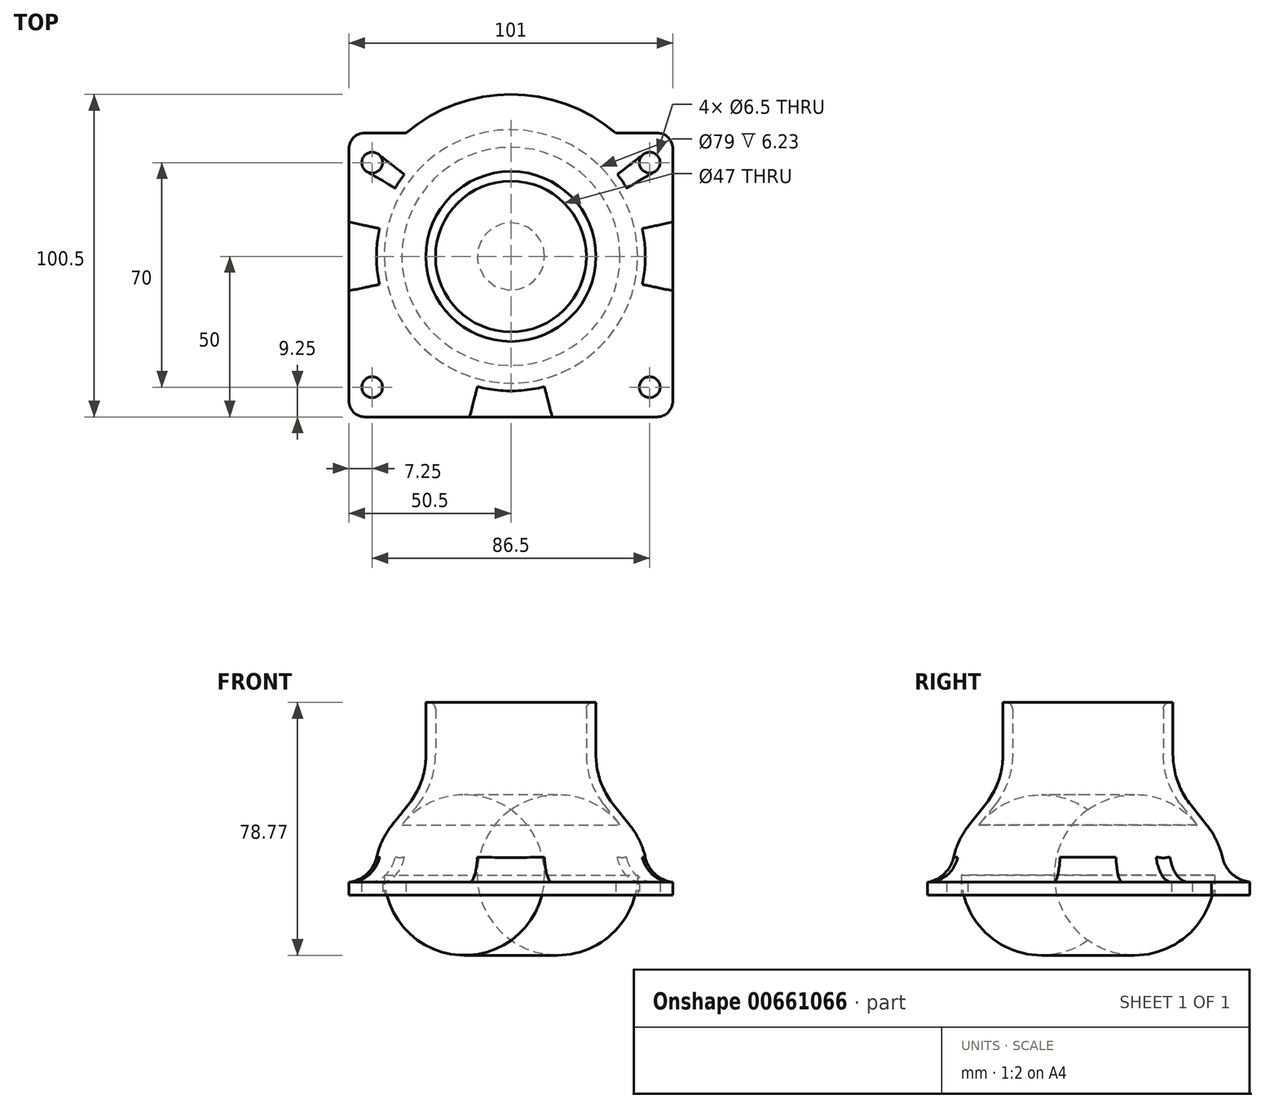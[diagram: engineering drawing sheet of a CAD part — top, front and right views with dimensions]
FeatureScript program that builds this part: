
annotation { "Feature Type Name" : "Feature", "Feature Type Description" : "" }
export const myFeature = defineFeature(function(context is Context, id is Id, definition is map)
    precondition{}
    {
        {
            assignVariable(context, id + "F0", {"name" : "baseTh", "anyValue" : 4});
        }
        {
            var Q0;
            Q0=qCreatedBy(makeId("Top.planeOp"),FACE);
            var sketch = newSketch(context, id + "F1", { "sketchPlane" : qUnion([Q0])});
            skLineSegment(sketch, "E0.bottom", {"start": v(45.5, -44.25) * mm, "end": v(-45.5, -44.25) * mm});
            skLineSegment(sketch, "E0.top", {"start": v(45.5, 44.25) * mm, "end": v(32.68, 44.25) * mm});
            skLineSegment(sketch, "E0.left", {"start": v(50.5, -39.25) * mm, "end": v(50.5, 39.25) * mm});
            skLineSegment(sketch, "E0.right", {"start": v(-50.5, -39.25) * mm, "end": v(-50.5, 39.25) * mm});
            skPoint(sketch, "E0.middle", {"position": v(0, 0) * mm});
            skLineSegment(sketch, "E1.bottom", {"start": v(43.25, -35) * mm, "end": v(-43.25, -35) * mm, "construction": true});
            skLineSegment(sketch, "E1.top", {"start": v(43.25, 35) * mm, "end": v(-43.25, 35) * mm, "construction": true});
            skLineSegment(sketch, "E1.left", {"start": v(43.25, -35) * mm, "end": v(43.25, 35) * mm, "construction": true});
            skLineSegment(sketch, "E1.right", {"start": v(-43.25, -35) * mm, "end": v(-43.25, 35) * mm, "construction": true});
            skCircle(sketch, "E2", {"center": v(-43.25, 35) * mm, "radius": 3.25 * mm});
            skCircle(sketch, "E3", {"center": v(-43.25, -35) * mm, "radius": 3.25 * mm});
            skCircle(sketch, "E4", {"center": v(43.25, -35) * mm, "radius": 3.25 * mm});
            skCircle(sketch, "E5", {"center": v(43.25, 35) * mm, "radius": 3.25 * mm});
            skLineSegment(sketch, "E6", {"start": v(0, -35) * mm, "end": v(0, 5.75) * mm, "construction": true});
            skCircle(sketch, "E7", {"center": v(0, 5.75) * mm, "radius": 39.5 * mm});
            skCircle(sketch, "E8", {"center": v(0, 5.75) * mm, "radius": 42 * mm});
            skCircle(sketch, "E9", {"center": v(0, 5.75) * mm, "radius": 45.5 * mm});
            skArc(sketch, "E10", {"start": v(43.3, 31.75) * mm, "mid": v(43.27, 31.79) * mm, "end": v(43.25, 31.82) * mm});
            skArc(sketch, "E11.trimOffspring", {"start": v(-43.25, 31.82) * mm, "mid": v(-43.27, 31.79) * mm, "end": v(-43.3, 31.75) * mm});
            skArc(sketch, "E12.trimOffspring", {"start": v(32.68, 44.25) * mm, "mid": v(0, 56.25) * mm, "end": v(-32.68, 44.25) * mm});
            skPoint(sketch, "E13.visualSharp", {"position": v(-50.5, 44.25) * mm});
            skArc(sketch, "E13.filletArc", {"start": v(-45.5, 44.25) * mm, "mid": v(-49.04, 42.79) * mm, "end": v(-50.5, 39.25) * mm});
            skPoint(sketch, "E14.visualSharp", {"position": v(-50.5, -44.25) * mm});
            skArc(sketch, "E14.filletArc", {"start": v(-50.5, -39.25) * mm, "mid": v(-49.04, -42.79) * mm, "end": v(-45.5, -44.25) * mm});
            skPoint(sketch, "E15.visualSharp", {"position": v(50.5, -44.25) * mm});
            skArc(sketch, "E15.filletArc", {"start": v(45.5, -44.25) * mm, "mid": v(49.04, -42.79) * mm, "end": v(50.5, -39.25) * mm});
            skPoint(sketch, "E16.visualSharp", {"position": v(50.5, 44.25) * mm});
            skArc(sketch, "E16.filletArc", {"start": v(50.5, 39.25) * mm, "mid": v(49.04, 42.79) * mm, "end": v(45.5, 44.25) * mm});
            skLineSegment(sketch, "E17.trimOffspring", {"start": v(-32.68, 44.25) * mm, "end": v(-45.5, 44.25) * mm});
            skSolve(sketch);
        }
        {
            var Q0;
            Q0=qCreatedBy(makeId("Front.planeOp"),FACE);
            cPlane(context, id + "F2", {"entities" : qUnion([Q0]), "cplaneType" : CPlaneType.OFFSET, "offset" : 5.75 * mm, "oppositeDirection" : true, "width" : 150 * mm, "height" : 150 * mm});
        }
        {
            var Q0;
            Q0=makeQuery(id+"F1.imprint","IMPRINT",FACE,{"disambiguationData":[TD([[makeQuery(id+"F1.imprint","IMPRINT",EDGE,{"derivedFrom":sQuery(id+"F1.wireOp",EDGE,"E0.bottom")}),-1.0]])]});
            var Q1;
            Q1=makeQuery(id+"F1.imprint","IMPRINT",FACE,{"disambiguationData":[TD([[makeQuery(id+"F1.imprint","IMPRINT",EDGE,{"derivedFrom":sQuery(id+"F1.wireOp",EDGE,"E8")}),-1.0]])]});
            var Q2;
            Q2=makeQuery(id+"F1.imprint","IMPRINT",FACE,{"disambiguationData":[TD([[makeQuery(id+"F1.imprint","IMPRINT",EDGE,{"derivedFrom":sQuery(id+"F1.wireOp",EDGE,"E7")}),-1.0]])]});
            extrude(context, id + "F3", {"entities" : qUnion([Q0, Q1, Q2]), "depth" : (getVariable(context, 'baseTh')) * mm, "offsetDistance" : 25 * mm});
        }
        {
            var Q0;
            Q0=qCreatedBy(id+"F2.planeOp",FACE);
            var sketch = newSketch(context, id + "F4", { "sketchPlane" : qUnion([Q0])});
            skLineSegment(sketch, "E18", {"start": v(0, 0) * mm, "end": v(-39.5, 0) * mm, "construction": true});
            skLineSegment(sketch, "E19", {"start": v(-39.5, 0) * mm, "end": v(-42.5, 0) * mm});
            skLineSegment(sketch, "E20", {"start": v(-39.5, 0) * mm, "end": v(-39.5, 15) * mm});
            skLineSegment(sketch, "E21", {"start": v(-42.5, 0) * mm, "end": v(-42.5, 15) * mm});
            skLineSegment(sketch, "E22", {"start": v(0, 0) * mm, "end": v(0, 60) * mm, "construction": true});
            skLineSegment(sketch, "E23", {"start": v(0, 60) * mm, "end": v(-23.5, 60) * mm, "construction": true});
            skLineSegment(sketch, "E24", {"start": v(-23.5, 60) * mm, "end": v(-26.5, 60) * mm});
            skLineSegment(sketch, "E25", {"start": v(-23.5, 60) * mm, "end": v(-23.5, 35) * mm});
            skLineSegment(sketch, "E26", {"start": v(-26.5, 60) * mm, "end": v(-26.5, 35) * mm});
            skLineSegment(sketch, "E27", {"start": v(-26.5, 35) * mm, "end": v(-42.5, 15) * mm});
            skLineSegment(sketch, "E28", {"start": v(-23.5, 35) * mm, "end": v(-39.5, 15) * mm});
            skSolve(sketch);
        }
        {
            var Q0;
            Q0=makeQuery(id+"F4.imprint","IMPRINT",FACE,{"disambiguationData":[TD([[makeQuery(id+"F4.imprint","IMPRINT",EDGE,{"derivedFrom":sQuery(id+"F4.wireOp",EDGE,"E19")}),-1.0]])]});
            var Q1;
            Q1=sQuery(id+"F4.wireOp",EDGE,"E22");
            revolve(context, id + "F5", {"operationType" : NewBodyOperationType.ADD, "entities" : qUnion([Q0]), "axis" : qUnion([Q1]), "revolveType" : RevolveType.FULL});
        }
        {
            var Q0;
            Q0=makeQuery(id+"F5.opRevolve","SWEPT_EDGE",EDGE,{"disambiguationData":[OSD([sQuery(id+"F4.wireOp",EDGE,"E24"),sQuery(id+"F4.wireOp",EDGE,"E25")])]});
            fillet(context, id + "F6", {"entities" : qUnion([Q0]), "radius" : 2 * mm, "tangentPropagation" : true, "allowEdgeOverflow" : false});
        }
        {
            var Q0;
            Q0=makeQuery(id+"F5.opRevolve","SWEPT_EDGE",EDGE,{"disambiguationData":[OSD([sQuery(id+"F4.wireOp",EDGE,"E26"),sQuery(id+"F4.wireOp",EDGE,"E27")])]});
            var Q1;
            Q1=makeQuery(id+"F5.opRevolve","SWEPT_EDGE",EDGE,{"disambiguationData":[OSD([sQuery(id+"F4.wireOp",EDGE,"E21"),sQuery(id+"F4.wireOp",EDGE,"E27")])]});
            var Q2;
            Q2=makeQuery(id+"F5.opRevolve","SWEPT_EDGE",EDGE,{"disambiguationData":[OSD([sQuery(id+"F4.wireOp",EDGE,"E25"),sQuery(id+"F4.wireOp",EDGE,"E28")])]});
            var Q3;
            Q3=makeQuery(id+"F5.opRevolve","SWEPT_EDGE",EDGE,{"disambiguationData":[OSD([sQuery(id+"F4.wireOp",EDGE,"E20"),sQuery(id+"F4.wireOp",EDGE,"E28")])]});
            fillet(context, id + "F7", {"entities" : qUnion([Q0, Q1, Q2, Q3]), "radius" : 25 * mm, "tangentPropagation" : true, "allowEdgeOverflow" : false});
        }
        {
            var Q0;
            Q0=makeQuery(id+"F5.boolean.opBoolean","INTERSECT",EDGE,{"derivedFrom":[makeQuery(id+"F3.opExtrude","CAP_FACE",FACE,{"disambiguationData":[OSD([sQuery(id+"F1.wireOp",EDGE,"E0.bottom"),sQuery(id+"F1.wireOp",EDGE,"E0.top"),sQuery(id+"F1.wireOp",EDGE,"E0.left"),sQuery(id+"F1.wireOp",EDGE,"E0.right"),sQuery(id+"F1.wireOp",EDGE,"E2"),sQuery(id+"F1.wireOp",EDGE,"E3"),sQuery(id+"F1.wireOp",EDGE,"E4"),sQuery(id+"F1.wireOp",EDGE,"E5"),sQuery(id+"F1.wireOp",EDGE,"E7"),sQuery(id+"F1.wireOp",EDGE,"E12.trimOffspring"),sQuery(id+"F1.wireOp",EDGE,"E13.filletArc"),sQuery(id+"F1.wireOp",EDGE,"E14.filletArc"),sQuery(id+"F1.wireOp",EDGE,"E15.filletArc"),sQuery(id+"F1.wireOp",EDGE,"E16.filletArc"),sQuery(id+"F1.wireOp",EDGE,"E17.trimOffspring")])],"isStart":false}),makeQuery(id+"F5.opRevolve","SWEPT_FACE",FACE,{"disambiguationData":[OSD([sQuery(id+"F4.wireOp",EDGE,"E21")])]})]});
            fillet(context, id + "F8", {"entities" : qUnion([Q0]), "radius" : 10 * mm, "tangentPropagation" : true, "allowEdgeOverflow" : false});
        }
    });
